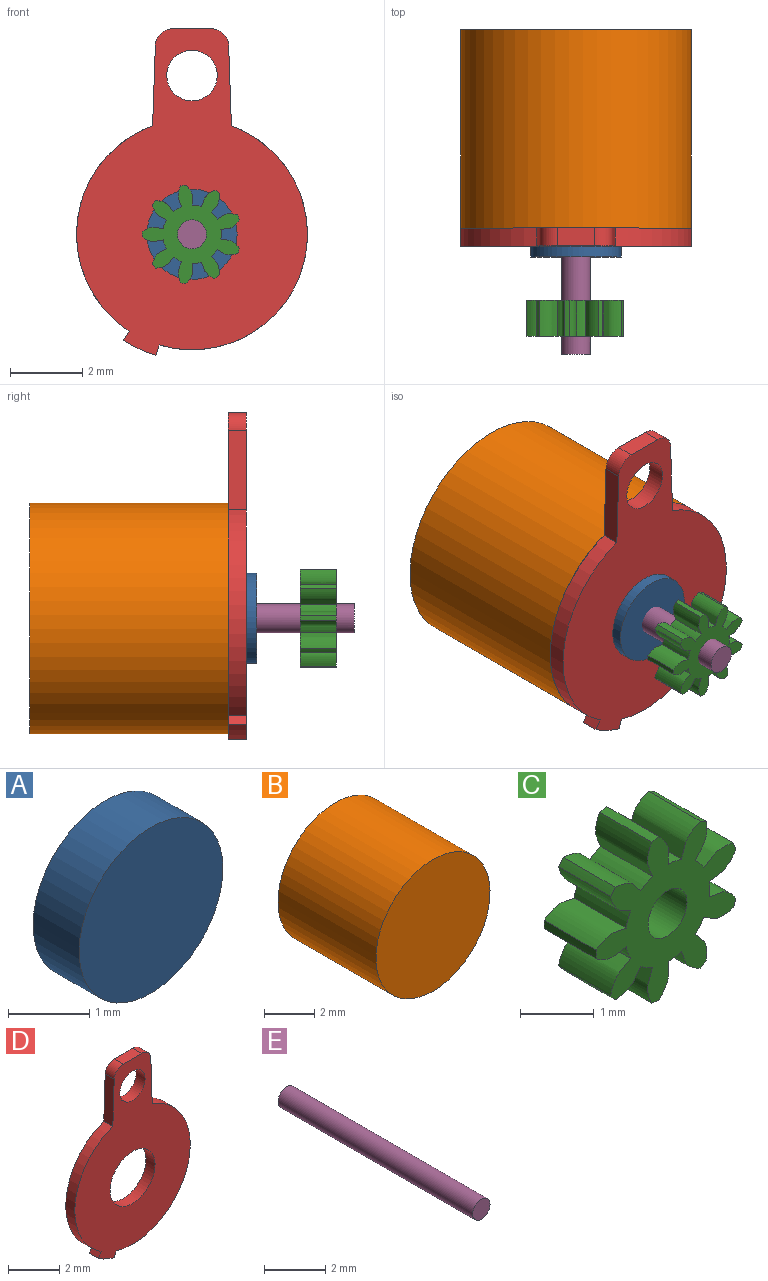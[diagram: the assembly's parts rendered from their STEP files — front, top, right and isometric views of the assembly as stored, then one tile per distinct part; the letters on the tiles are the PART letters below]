
ASSEMBLY  parts=5 mates=4
PART A: 3 faces, bbox 2.5x0.8x2.5 mm
  f0: cylinder r=1.25mm len=2.5mm, axis (0,1,0), area 6.3mm2, adj f1,f2
  f1: plane 2.5x2.5mm, normal (0,-1,0), area 4.9mm2, adj f0
  f2: plane 2.5x2.5mm, normal (0,1,0), area 4.9mm2, adj f0
PART B: 3 faces, bbox 6.4x5.5x6.4 mm
  f0: plane 6.4x6.4mm, normal (0,-1,0), area 32.2mm2, adj f2
  f1: plane 6.4x6.4mm, normal (0,1,0), area 32.2mm2, adj f2
  f2: cylinder r=3.2mm len=6.4mm, axis (0,-1,0), area 110.6mm2, adj f0,f1
PART C: 39 faces, bbox 2.7x1x2.7 mm
  f0: extruded ~1x0.51mm, area 0.6mm2, adj f1,f36,f37,f38
  f1: cylinder r=0.81mm len=1mm, axis (0,1,0), area 0.3mm2, adj f0,f2,f37,f38
  f2: extruded ~1x0.51mm, area 0.6mm2, adj f1,f3,f37,f38
  f3: cylinder r=1.38mm len=1mm, axis (0,1,0), area 0.1mm2, adj f2,f4,f37,f38
  f4: extruded ~1x0.57mm, area 0.6mm2, adj f3,f5,f37,f38
  f5: cylinder r=0.81mm len=1mm, axis (0,1,0), area 0.3mm2, adj f4,f6,f37,f38
  f6: extruded ~1x0.54mm, area 0.6mm2, adj f5,f7,f37,f38
  f7: cylinder r=1.38mm len=1mm, axis (0,1,0), area 0.1mm2, adj f6,f8,f37,f38
  f8: extruded ~1x0.46mm, area 0.6mm2, adj f7,f9,f37,f38
  f9: cylinder r=0.81mm len=1mm, axis (0,1,0), area 0.3mm2, adj f8,f10,f37,f38
  f10: extruded ~1x0.55mm, area 0.6mm2, adj f9,f11,f37,f38
  f11: cylinder r=1.38mm len=1mm, axis (0,1,0), area 0.1mm2, adj f10,f12,f37,f38
  f12: extruded ~1x0.58mm, area 0.6mm2, adj f11,f13,f37,f38
  f13: cylinder r=0.81mm len=1mm, axis (0,1,0), area 0.3mm2, adj f12,f14,f37,f38
  f14: extruded ~1x0.49mm, area 0.6mm2, adj f13,f15,f37,f38
  f15: cylinder r=1.38mm len=1mm, axis (0,1,0), area 0.1mm2, adj f14,f16,f37,f38
  f16: extruded ~1x0.43mm, area 0.6mm2, adj f15,f17,f37,f38
  f17: cylinder r=0.81mm len=1mm, axis (0,1,0), area 0.3mm2, adj f16,f18,f37,f38
  f18: extruded ~1x0.58mm, area 0.6mm2, adj f17,f19,f37,f38
  f19: cylinder r=1.38mm len=1mm, axis (0,1,0), area 0.1mm2, adj f18,f20,f37,f38
  f20: extruded ~1x0.58mm, area 0.6mm2, adj f19,f21,f37,f38
  f21: cylinder r=0.81mm len=1mm, axis (0,1,0), area 0.3mm2, adj f20,f22,f37,f38
  f22: extruded ~1x0.43mm, area 0.6mm2, adj f21,f23,f37,f38
  f23: cylinder r=1.38mm len=1mm, axis (0,1,0), area 0.1mm2, adj f22,f24,f37,f38
  f24: extruded ~1x0.49mm, area 0.6mm2, adj f23,f25,f37,f38
  f25: cylinder r=0.81mm len=1mm, axis (0,1,0), area 0.3mm2, adj f24,f26,f37,f38
  f26: extruded ~1x0.58mm, area 0.6mm2, adj f25,f27,f37,f38
  f27: cylinder r=1.38mm len=1mm, axis (0,1,0), area 0.1mm2, adj f26,f28,f37,f38
  f28: extruded ~1x0.55mm, area 0.6mm2, adj f27,f29,f37,f38
  f29: cylinder r=0.81mm len=1mm, axis (0,1,0), area 0.3mm2, adj f28,f30,f37,f38
  f30: extruded ~1x0.46mm, area 0.6mm2, adj f29,f31,f37,f38
  f31: cylinder r=1.38mm len=1mm, axis (0,1,0), area 0.1mm2, adj f30,f32,f37,f38
  f32: extruded ~1x0.54mm, area 0.6mm2, adj f31,f33,f37,f38
  f33: cylinder r=0.81mm len=1mm, axis (0,1,0), area 0.3mm2, adj f32,f34,f37,f38
  f34: extruded ~1x0.57mm, area 0.6mm2, adj f33,f36,f37,f38
  f35: cylinder r=0.38mm len=1mm, axis (0,1,0), area 2.4mm2, adj f37,f38
  f36: cylinder r=1.38mm len=1mm, axis (0,1,0), area 0.1mm2, adj f0,f34,f37,f38
  f37: plane 2.75x2.71mm, normal (0,-1,0), area 3.3mm2, adj f0,f1,f2,f3,f4,f5,f6,f7
  f38: plane 2.75x2.71mm, normal (0,1,0), area 3.3mm2, adj f0,f1,f2,f3,f4,f5,f6,f7
PART D: 14 faces, bbox 6.4x0.5x9.1 mm
  f0: plane 2.21x0.5mm, normal (-1,0,0.03), area 1.1mm2, adj f1,f9,f12,f13
  f1: cylinder r=3.2mm len=5.69mm, axis (0,1,0), area 3.5mm2, adj f0,f2,f12,f13
  f2: plane 0.5x0.25mm, normal (-0.84,0,0.55), area 0.1mm2, adj f1,f3,f12,f13
  f3: cylinder r=3.5mm len=0.91mm, axis (0,1,0), area 0.5mm2, adj f2,f4,f12,f13
  f4: plane 0.5x0.29mm, normal (0.96,0,-0.29), area 0.1mm2, adj f3,f5,f12,f13
  f5: cylinder r=3.2mm len=6.21mm, axis (0,1,0), area 4.9mm2, adj f4,f6,f12,f13
  f6: plane 2.21x0.5mm, normal (1,0,0.03), area 1.1mm2, adj f5,f7,f12,f13
  f7: cylinder r=0.5mm len=0.5mm, axis (0,1,0), area 0.4mm2, adj f6,f8,f12,f13
  f8: plane 1.03x0.5mm, normal (0,0,1), area 0.5mm2, adj f7,f9,f12,f13
  f9: cylinder r=0.5mm len=0.5mm, axis (0,1,0), area 0.4mm2, adj f0,f8,f12,f13
  f10: cylinder r=0.7mm len=1.4mm, axis (0,1,0), area 2.2mm2, adj f12,f13
  f11: cylinder r=1.25mm len=2.5mm, axis (0,1,0), area 3.9mm2, adj f12,f13
  f12: plane 9.05x6.4mm, normal (0,-1,0), area 31.3mm2, adj f0,f1,f2,f3,f4,f5,f6,f7
  f13: plane 9.05x6.4mm, normal (0,1,0), area 31.3mm2, adj f0,f1,f2,f3,f4,f5,f6,f7
PART E: 3 faces, bbox 0.8x9x0.8 mm
  f0: plane 0.8x0.8mm, normal (0,-1,0), area 0.5mm2, adj f1
  f1: cylinder r=0.4mm len=9mm, axis (0,1,0), area 22.6mm2, adj f0,f2
  f2: plane 0.8x0.8mm, normal (0,1,0), area 0.5mm2, adj f1
PLACE A at identity
PLACE B at identity fixed
PLACE C t=(0,-4.75,0)mm
PLACE D at identity
PLACE E at identity
MATE fastened A.f0 <-> B.f2  axis (0,1,0) through (0,-2.75,0)mm
MATE fastened B.f2 <-> D.f11  axis (0,-1,0) through (0,-2.75,0)mm
MATE fastened C.f3 <-> E.f1  axis (0,-1,0) through (0,-5.75,0)mm
MATE fastened E.f1 <-> B.f2  axis (0,1,0) through (0,2.75,0)mm
